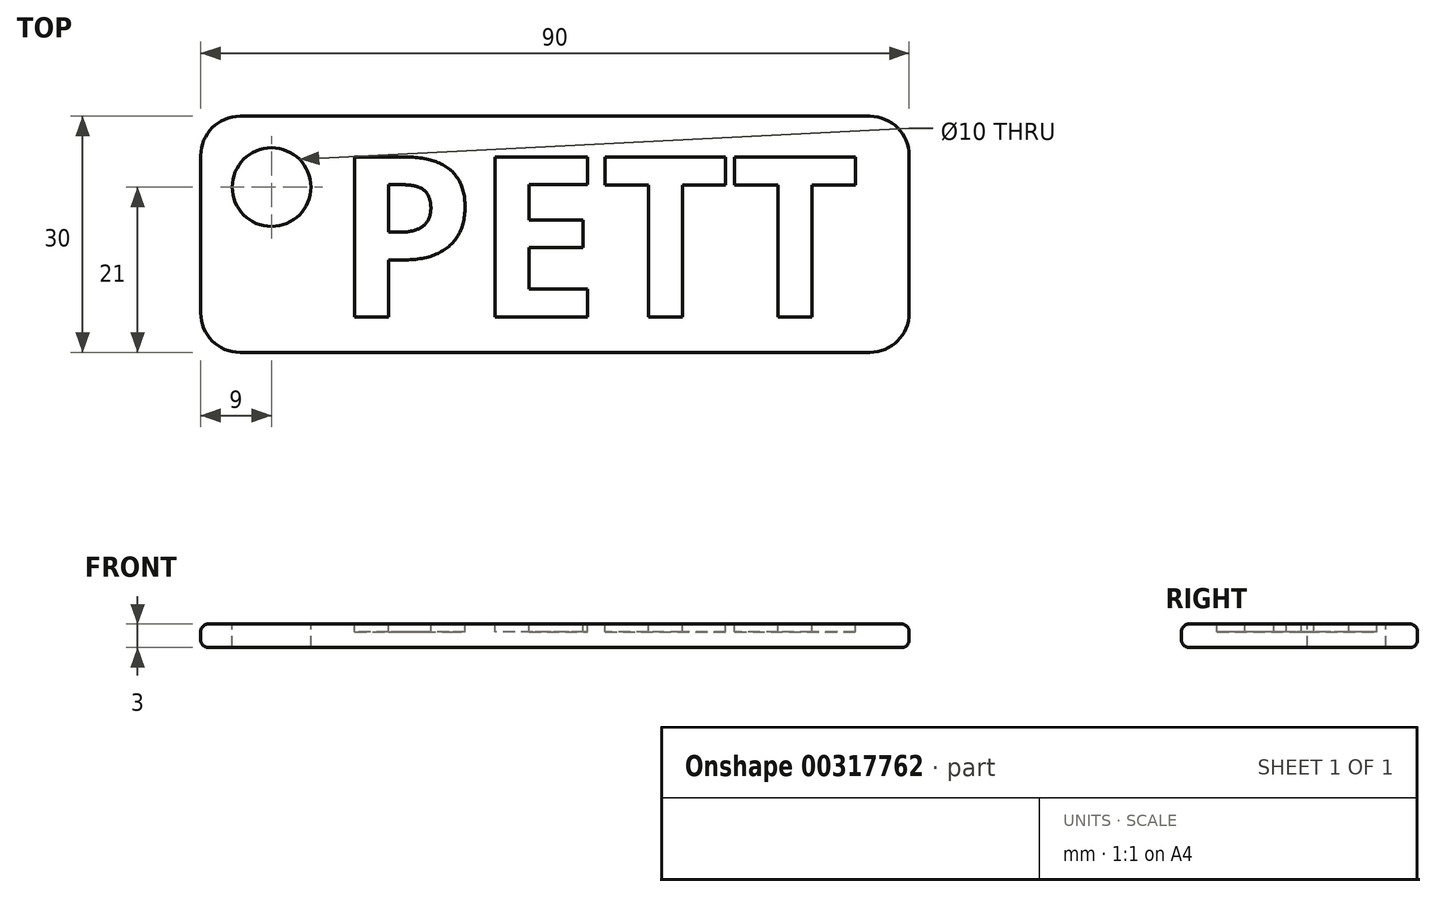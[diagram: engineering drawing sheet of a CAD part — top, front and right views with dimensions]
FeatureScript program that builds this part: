
annotation { "Feature Type Name" : "Feature", "Feature Type Description" : "" }
export const myFeature = defineFeature(function(context is Context, id is Id, definition is map)
    precondition{}
    {
        {
            var Q0;
            Q0=qCreatedBy(makeId("Top.planeOp"),FACE);
            var sketch = newSketch(context, id + "F0", { "sketchPlane" : qUnion([Q0])});
            skLineSegment(sketch, "E0.bottom", {"start": v(-45, 15) * mm, "end": v(45, 15) * mm});
            skLineSegment(sketch, "E0.top", {"start": v(-45, -15) * mm, "end": v(45, -15) * mm});
            skLineSegment(sketch, "E0.left", {"start": v(-45, 15) * mm, "end": v(-45, -15) * mm});
            skLineSegment(sketch, "E0.right", {"start": v(45, 15) * mm, "end": v(45, -15) * mm});
            skLineSegment(sketch, "E1", {"start": v(-45, 15) * mm, "end": v(45, -15) * mm, "construction": true});
            skSolve(sketch);
        }
        {
            var Q0;
            Q0=makeQuery(id+"F0.imprint","IMPRINT",FACE,{"disambiguationData":[TD([[makeQuery(id+"F0.imprint","IMPRINT",EDGE,{"derivedFrom":sQuery(id+"F0.wireOp",EDGE,"E0.bottom")}),-1.0]])]});
            extrude(context, id + "F1", {"entities" : qUnion([Q0]), "depth" : 3 * mm});
        }
        {
            var Q0;
            Q0=makeQuery(id+"F1.opExtrude","CAP_FACE",FACE,{"disambiguationData":[OSD([sQuery(id+"F0.wireOp",EDGE,"E0.bottom"),sQuery(id+"F0.wireOp",EDGE,"E0.top"),sQuery(id+"F0.wireOp",EDGE,"E0.left"),sQuery(id+"F0.wireOp",EDGE,"E0.right")])],"isStart":false});
            var Q1;
            Q1=makeQuery(id+"F1.opExtrude","CAP_FACE",FACE,{"disambiguationData":[OSD([sQuery(id+"F0.wireOp",EDGE,"E0.bottom"),sQuery(id+"F0.wireOp",EDGE,"E0.top"),sQuery(id+"F0.wireOp",EDGE,"E0.left"),sQuery(id+"F0.wireOp",EDGE,"E0.right")])],"isStart":true});
            fillet(context, id + "F2", {"entities" : qUnion([Q0, Q1]), "radius" : 1 * mm, "tangentPropagation" : true, "allowEdgeOverflow" : false});
        }
        {
            var Q0;
            Q0=makeQuery(id+"F1.opExtrude","SWEPT_EDGE",EDGE,{"disambiguationData":[OSD([sQuery(id+"F0.wireOp",EDGE,"E0.top"),sQuery(id+"F0.wireOp",EDGE,"E0.right")])]});
            var Q1;
            Q1=makeQuery(id+"F1.opExtrude","SWEPT_EDGE",EDGE,{"disambiguationData":[OSD([sQuery(id+"F0.wireOp",EDGE,"E0.bottom"),sQuery(id+"F0.wireOp",EDGE,"E0.right")])]});
            var Q2;
            Q2=makeQuery(id+"F1.opExtrude","SWEPT_EDGE",EDGE,{"disambiguationData":[OSD([sQuery(id+"F0.wireOp",EDGE,"E0.bottom"),sQuery(id+"F0.wireOp",EDGE,"E0.left")])]});
            var Q3;
            Q3=makeQuery(id+"F1.opExtrude","SWEPT_EDGE",EDGE,{"disambiguationData":[OSD([sQuery(id+"F0.wireOp",EDGE,"E0.top"),sQuery(id+"F0.wireOp",EDGE,"E0.left")])]});
            fillet(context, id + "F3", {"entities" : qUnion([Q0, Q1, Q2, Q3]), "radius" : 5 * mm, "tangentPropagation" : true, "allowEdgeOverflow" : false});
        }
        {
            var Q0;
            {var subQ0=sQuery(id+"F0.wireOp",EDGE,"E0.left");var subQ2=sQuery(id+"F0.wireOp",EDGE,"E0.bottom");var subQ4=sQuery(id+"F0.wireOp",EDGE,"E0.right");var subQ6=sQuery(id+"F0.wireOp",EDGE,"E0.top");Q0=makeQuery(id+"FmQCBBX3Ub0qneL_1.boolean.opBoolean","SPLIT",FACE,{"disambiguationData":[TD([makeQuery(id+"FmQCBBX3Ub0qneL_1.opExtrude","SWEPT_FACE",FACE,{"disambiguationData":[OSD([sQuery(id+"FOCoeRmDbjhRCuz_1.wireOp",EDGE,"4a1fb44a-e7be-4e23-9449-000d953c446c.sketch_text.stroke-0")])]})])],"derivedFrom":makeQuery(id+"F1.opExtrude","CAP_FACE",FACE,{"disambiguationData":[OSD([subQ2,subQ6,subQ0,subQ4])],"isStart":false})});}
            var sketch = newSketch(context, id + "F4", { "sketchPlane" : qUnion([Q0])});
            skCircle(sketch, "E2", {"center": v(-36, 6) * mm, "radius": 5 * mm});
            skSolve(sketch);
        }
        {
            var Q0;
            Q0=qSketchRegion(id+"F4",true);
            extrude(context, id + "F5", {"entities" : qUnion([Q0]), "operationType" : NewBodyOperationType.REMOVE, "oppositeDirection" : true, "depth" : 3 * mm});
        }
        {
            var Q0;
            Q0=makeQuery(id+"F1.opExtrude","CAP_FACE",FACE,{"disambiguationData":[OSD([sQuery(id+"F0.wireOp",EDGE,"E0.bottom"),sQuery(id+"F0.wireOp",EDGE,"E0.top"),sQuery(id+"F0.wireOp",EDGE,"E0.left"),sQuery(id+"F0.wireOp",EDGE,"E0.right")])],"isStart":false});
            var sketch = newSketch(context, id + "F6", { "sketchPlane" : qUnion([Q0])});
            skText(sketch, "E3", { "text": "PETT", "fontName": "OpenSans-Bold.ttf"});
            const initialGuessF6  = {"E3": [-0.028, -0.01048, 1, 0, 0.02048]};
            skSetInitialGuess(sketch, initialGuessF6);
            skSolve(sketch);
        }
        {
            var Q0;
            Q0=qSketchRegion(id+"F6",true);
            extrude(context, id + "F7", {"entities" : qUnion([Q0]), "operationType" : NewBodyOperationType.REMOVE, "oppositeDirection" : true, "depth" : 1 * mm});
        }
    });
